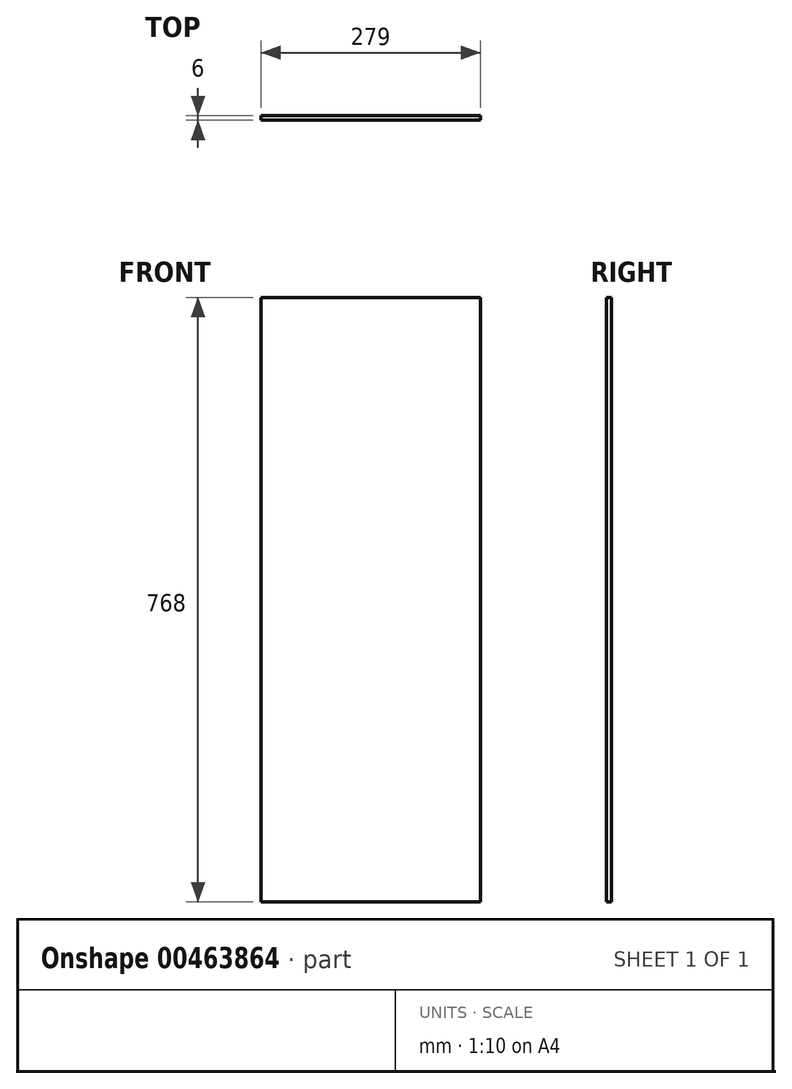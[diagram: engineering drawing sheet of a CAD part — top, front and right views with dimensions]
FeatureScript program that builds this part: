
annotation { "Feature Type Name" : "Feature", "Feature Type Description" : "" }
export const myFeature = defineFeature(function(context is Context, id is Id, definition is map)
    precondition{}
    {
        {
            var Q0;
            Q0=qCreatedBy(makeId("Front.planeOp"),FACE);
            var sketch = newSketch(context, id + "F0", { "sketchPlane" : qUnion([Q0])});
            skLineSegment(sketch, "E0.bottom", {"start": v(0, 0) * mm, "end": v(279, 0) * mm});
            skLineSegment(sketch, "E0.top", {"start": v(0, 768) * mm, "end": v(279, 768) * mm});
            skLineSegment(sketch, "E0.left", {"start": v(0, 0) * mm, "end": v(0, 768) * mm});
            skLineSegment(sketch, "E0.right", {"start": v(279, 0) * mm, "end": v(279, 768) * mm});
            skSolve(sketch);
        }
        {
            var Q0;
            Q0 = qSketchRegion(id + "F0", true);
            extrude(context, id + "F1", {"entities" : qUnion([Q0]), "depth" : 6 * mm});
        }
    });
